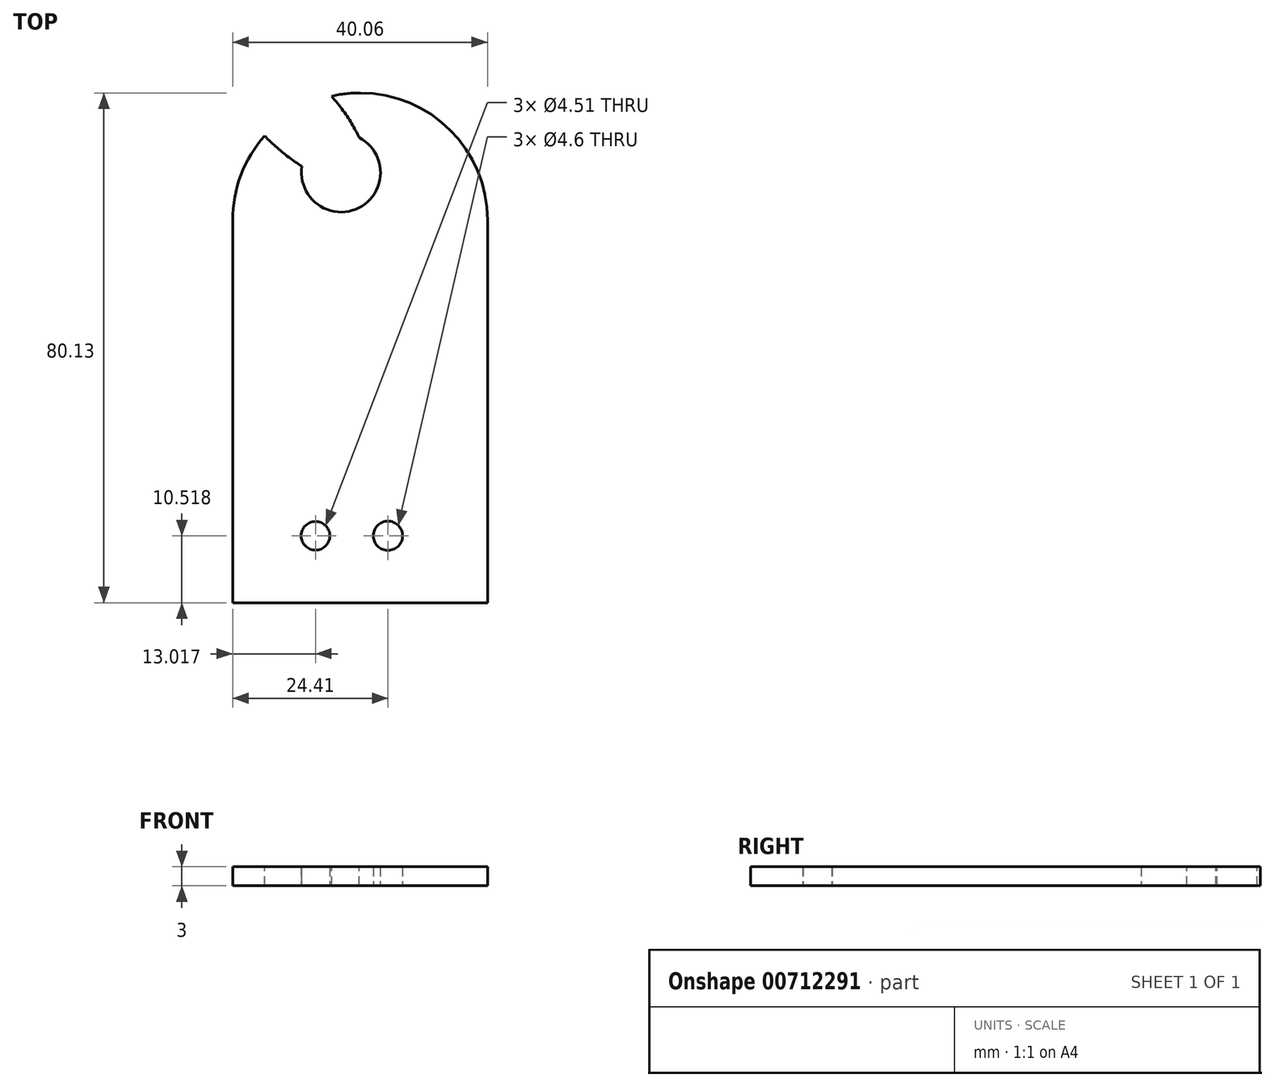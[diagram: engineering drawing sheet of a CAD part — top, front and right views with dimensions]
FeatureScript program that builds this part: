
annotation { "Feature Type Name" : "Feature", "Feature Type Description" : "" }
export const myFeature = defineFeature(function(context is Context, id is Id, definition is map)
    precondition{}
    {
        {
            var Q0;
            Q0=qCreatedBy(makeId("Top.planeOp"),FACE);
            var sketch = newSketch(context, id + "F0", { "sketchPlane" : qUnion([Q0])});
            skLineSegment(sketch, "E0.bottom", {"start": v(-24.41, -24.29) * mm, "end": v(15.65, -24.29) * mm});
            skLineSegment(sketch, "E0.top", {"start": v(-24.41, 55.84) * mm, "end": v(15.65, 55.84) * mm});
            skLineSegment(sketch, "E0.left", {"start": v(-24.41, -24.29) * mm, "end": v(-24.41, 55.84) * mm});
            skLineSegment(sketch, "E0.right", {"start": v(15.65, -24.29) * mm, "end": v(15.65, 55.84) * mm});
            skCircle(sketch, "E1", {"center": v(-7.39, 43.32) * mm, "radius": 6.2 * mm});
            skCircle(sketch, "E2", {"center": v(-11.4, -13.77) * mm, "radius": 2.25 * mm});
            skCircle(sketch, "E3", {"center": v(0, -13.77) * mm, "radius": 2.3 * mm});
            skSolve(sketch);
        }
        {
            var Q0;
            Q0=makeQuery(id+"F0.imprint","IMPRINT",FACE,{"disambiguationData":[TD([[makeQuery(id+"F0.imprint","IMPRINT",EDGE,{"derivedFrom":sQuery(id+"F0.wireOp",EDGE,"E0.bottom")}),1.0]])]});
            extrude(context, id + "F1", {"entities" : qUnion([Q0]), "depth" : 3 * mm, "offsetDistance" : 25 * mm});
        }
        {
            var Q0;
            Q0=makeQuery(id+"F1.opExtrude","SWEPT_EDGE",EDGE,{"disambiguationData":[OSD([sQuery(id+"F0.wireOp",EDGE,"E0.top"),sQuery(id+"F0.wireOp",EDGE,"E0.right")])]});
            var Q1;
            Q1=makeQuery(id+"F1.opExtrude","SWEPT_EDGE",EDGE,{"disambiguationData":[OSD([sQuery(id+"F0.wireOp",EDGE,"E0.top"),sQuery(id+"F0.wireOp",EDGE,"E0.left")])]});
            fillet(context, id + "F2", {"entities" : qUnion([Q0, Q1]), "radius" : 20 * mm, "tangentPropagation" : true, "allowEdgeOverflow" : false});
        }
        {
            var Q0;
            Q0=makeQuery(id+"F1.opExtrude","CAP_FACE",FACE,{"disambiguationData":[OSD([sQuery(id+"F0.wireOp",EDGE,"E0.bottom"),sQuery(id+"F0.wireOp",EDGE,"E0.top"),sQuery(id+"F0.wireOp",EDGE,"E0.left"),sQuery(id+"F0.wireOp",EDGE,"E0.right"),sQuery(id+"F0.wireOp",EDGE,"E1")])],"isStart":false});
            var sketch = newSketch(context, id + "F3", { "sketchPlane" : qUnion([Q0])});
            skEllipse(sketch, "E4", {"center": v(-14.8, 52.93) * mm, "majorRadius": 14.6 * mm, "minorRadius": 5.97 * mm, "majorAxis": v(0.71, -0.7)});
            skSolve(sketch);
        }
        {
            var Q0;
            {var subQ0=sQuery(id+"F3.wireOp",EDGE,"E4");var subQ1=sQuery(id+"F0.wireOp",EDGE,"E0.left");var subQ2=sQuery(id+"F0.wireOp",EDGE,"E0.top");var subQ3=makeQuery(id+"F2.opFillet","BLEND_EDGE",EDGE,{"blendedFrom":[makeQuery(id+"F1.opExtrude","SWEPT_EDGE",EDGE,{"disambiguationData":[OSD([subQ2,subQ1])]}),makeQuery(id+"F1.opExtrude","CAP_FACE",FACE,{"disambiguationData":[OSD([sQuery(id+"F0.wireOp",EDGE,"E0.bottom"),subQ2,subQ1,sQuery(id+"F0.wireOp",EDGE,"E0.right"),sQuery(id+"F0.wireOp",EDGE,"E1")])],"isStart":false})],"blendedInto":[makeQuery(id+"F1.opExtrude","CAP_FACE",FACE,{"disambiguationData":[OSD([sQuery(id+"F0.wireOp",EDGE,"E0.bottom"),subQ2,subQ1,sQuery(id+"F0.wireOp",EDGE,"E0.right"),sQuery(id+"F0.wireOp",EDGE,"E1")])],"isStart":false})]});var subQ4=makeQuery(id+"F3.imprint","INTERSECT",VERTEX,{"disambiguationData":[OD(0.0)],"derivedFrom":[subQ3,subQ0]});Q0=makeQuery(id+"F3.imprint","IMPRINT",FACE,{"disambiguationData":[TD([[makeQuery(id+"F3.imprint","IMPRINT",EDGE,{"disambiguationData":[TD([[subQ4,-1.0]])],"derivedFrom":subQ0}),1.0]])]});}
            var Q1;
            {var subQ0=sQuery(id+"F3.wireOp",EDGE,"E4");var subQ1=sQuery(id+"F0.wireOp",EDGE,"E1");var subQ6=makeQuery(id+"F1.opExtrude","CAP_EDGE",EDGE,{"disambiguationData":[OSD([subQ1])],"isStart":false});var subQ7=makeQuery(id+"F3.imprint","INTERSECT",VERTEX,{"disambiguationData":[OD(0.0)],"derivedFrom":[subQ6,subQ0]});Q1=makeQuery(id+"F3.imprint","IMPRINT",FACE,{"disambiguationData":[TD([[makeQuery(id+"F3.imprint","IMPRINT",EDGE,{"disambiguationData":[TD([[subQ7,-1.0]])],"derivedFrom":subQ6}),-1.0]])]});}
            var Q2;
            {var subQ0=sQuery(id+"F3.wireOp",EDGE,"E4");var subQ1=makeQuery(id+"F1.opExtrude","CAP_EDGE",EDGE,{"disambiguationData":[OSD([sQuery(id+"F0.wireOp",EDGE,"E1")])],"isStart":false});var subQ2=makeQuery(id+"F3.imprint","INTERSECT",VERTEX,{"disambiguationData":[OD(0.0)],"derivedFrom":[subQ1,subQ0]});Q2=makeQuery(id+"F3.imprint","IMPRINT",FACE,{"disambiguationData":[TD([[makeQuery(id+"F3.imprint","IMPRINT",EDGE,{"disambiguationData":[TD([[subQ2,1.0]])],"derivedFrom":subQ0}),1.0]])]});}
            extrude(context, id + "F4", {"entities" : qUnion([Q0, Q1, Q2]), "operationType" : NewBodyOperationType.REMOVE, "oppositeDirection" : true, "depth" : 3 * mm, "offsetDistance" : 25 * mm});
        }
    });
